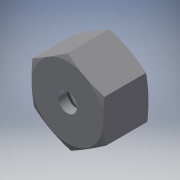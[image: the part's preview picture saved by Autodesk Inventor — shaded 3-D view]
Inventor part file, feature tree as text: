
AUTODESK INVENTOR PART (.ipt)
format: ipt  version: 2016 (Build 200138000, 138)  size: 147,968 bytes
history: native  units: in
note: dims shown in document units (in); Inventor stores cm internally (conversion verified against a paired STEP export)
features: sketch x4, plane x3, extrude x3, reference x2, thread x1, other x1, revolve x1, mirror x1
ambient origin geometry x8: Origin, YZ Plane, XZ Plane, XY Plane, X Axis, Y Axis, Z Axis, Center Point
bodies: Body1 (feature_tree)
feature tree (16):
  plane  "Work Plane3"
  extrude  "Extrusion2"  Depth=0.5in
  extrude  "Extrusion3"  Depth=0.375in TaperAngle=0.0deg
  extrude  "Extrusion4"  TaperAngle=90.0deg  [1 undecoded]
  thread  "Thread1"  [1 undecoded]
  plane  "Work Plane4"
  other  "Work Axis4"
  revolve  "Revolution2"  [1 undecoded]
  plane  "Work Plane5"
  mirror  "Mirror1"
  sketch  "Sketch6"  dims[d3=0.3125in d4=0.0in d5=0.5in]
  sketch  "Sketch7"  dims[d6=0.25in d7=-0.0123in d8=0.375in d9=0.0in]
  reference  "Reference1"
  sketch  "Sketch8"  dims[d10=0.392in d11=0.0in d12=90.0deg d13=0.045in]
  reference  "Reference2"
  sketch  "Sketch9"
note: 3 required parameter values undecoded (feature->parameter linkage not recoverable at this tier; creation-order binding heuristic only, values carry confidence <= 0.55)
